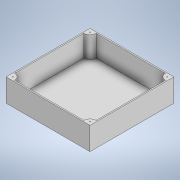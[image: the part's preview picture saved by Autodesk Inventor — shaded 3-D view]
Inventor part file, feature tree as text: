
AUTODESK INVENTOR PART (.ipt)
format: ipt  version: 2021 (Build 250183000, 183)  size: 140,800 bytes
history: native  units: mm
features: sketch x3, extrude x2, other x1, shell x1, hole x1
ambient origin geometry x8: Origin, YZ Plane, XZ Plane, XY Plane, X Axis, Y Axis, Z Axis, Center Point
bodies: Body1 (feature_tree)
feature tree (8):
  other  "Sólido1"
  extrude  "Extrusión1"  Depth=206.0mm
  shell  "Vaciado1"  Thickness=56.0mm
  extrude  "Extrusión2"  Depth=3.0mm
  hole  "Agujero1"  [1 undecoded]
  sketch  "Boceto1"  dims[d0=206.0mm d1=206.0mm d2=56.0mm d3=0.0mm]
  sketch  "Boceto2"  dims[d4=3.0mm d5=30.0mm]
  sketch  "Boceto3"  dims[d6=30.0mm d7=30.0mm d8=30.0mm d9=53.0mm d10=0.0mm d12=2.0mm d13=40.0mm d15=360.0deg d17=2.0mm d18=6.0mm d19=4.0mm d20=2.0mm d21=90.0deg d22=25.0mm d23=20.594885mm]
note: 1 required parameter value undecoded (feature->parameter linkage not recoverable at this tier; creation-order binding heuristic only, values carry confidence <= 0.55)
